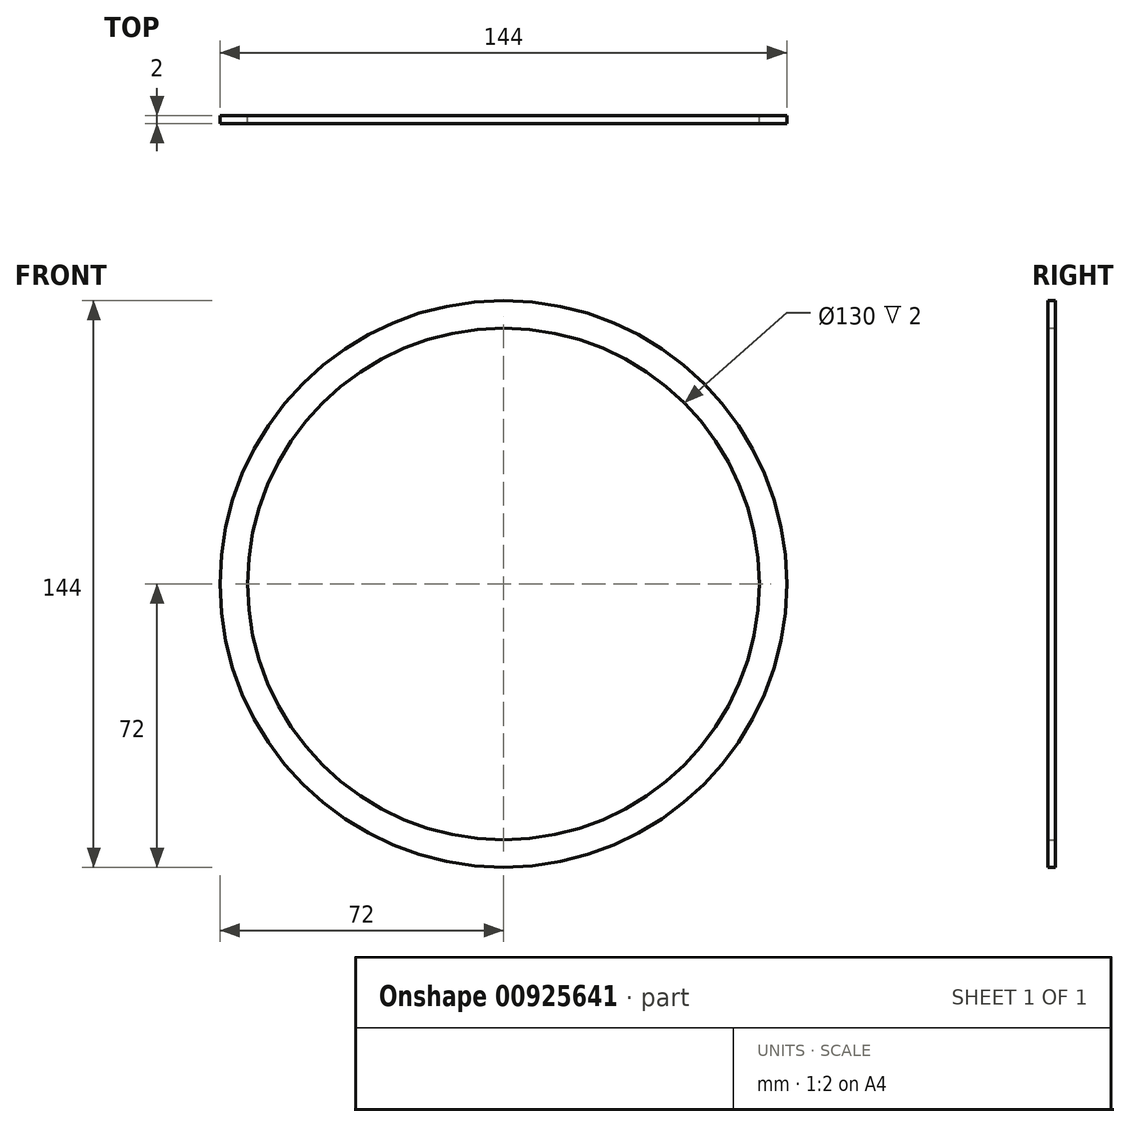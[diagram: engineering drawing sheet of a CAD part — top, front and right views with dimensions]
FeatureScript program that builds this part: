
annotation { "Feature Type Name" : "Feature", "Feature Type Description" : "" }
export const myFeature = defineFeature(function(context is Context, id is Id, definition is map)
    precondition{}
    {
        {
            var Q0;
            Q0=qCreatedBy(makeId("Front.planeOp"),FACE);
            var sketch = newSketch(context, id + "F0", { "sketchPlane" : qUnion([Q0])});
            skCircle(sketch, "E0", {"center": v(0, 0) * mm, "radius": 72 * mm});
            skCircle(sketch, "E1", {"center": v(0, 0) * mm, "radius": 65 * mm});
            skSolve(sketch);
        }
        {
            var Q0;
            Q0=makeQuery(id+"F0.imprint","IMPRINT",FACE,{"disambiguationData":[TD([[makeQuery(id+"F0.imprint","IMPRINT",EDGE,{"derivedFrom":sQuery(id+"F0.wireOp",EDGE,"E0")}),1.0]])]});
            extrude(context, id + "F1", {"entities" : qUnion([Q0]), "depth" : 2 * mm, "offsetDistance" : 25 * mm});
        }
    });
